# Revit family: Signalizator magnitokontaktnyy SMK-11
name_source: partatom
category: Датчики
units: mm (PartAtom-declared; Revit-internal decimal feet)

## family parameters
Всегда вертикально = Да
Заголовок OmniClass = Communication and Data Processing Equipment
На основе рабочей плоскости = Нет
Номер OmniClass = 23.85.50.17
Общий = Нет
При загрузке вырезать с полостями = Нет
Размер круглого соединителя = Использовать диаметр
Сохранять ориентацию аннотаций = Нет
Тип детали = Нормальный
Точка принадлежности помещению = Нет

## types (2) — shared parameters
ADSK_Единица измерения = шт.
ADSK_Завод-изготовитель = ООО НПП «МАГНИТО-КОНТАКТ»
ADSK_Материал = Пластик
ADSK_Обозначение = АТФЕ.425119.169 ПС
ADSK_Примечание = По устойчивости к климатическим воздействиям сигнализатор рассчитан для категории размещения III по ГОСТ 54455-2011 в диапазоне температур окружающего воздуха от -60°С до +60°С и относительной влажности до 98% при температуре +35°С без конденсации влаги.
ADSK_Размер_ДиаметрИзделия = 7 мм
ADSK_Размер_Длина = 22 мм
URL = https://m-kontakt.ru
Диапазон коммутируемого тока = от 0.005 до 0.25
Диапазон напряжений = от 0.05 до 72 (постоянного или переменного тока)
Длина вывода, м = 1 мм
Изготовитель = ООО НПП «МАГНИТО-КОНТАКТ»
Кабель = Да
Описание = Сигнализатор магнитоконтактный СМК-11 предназначен для применения в системах автоматики различных устройств, в технике бытового, коммерческого, медицинского, научного и промышленного назначений с выдачей сигнала, путем размыкания сухого контакта геркона, а так же в системах охранной или охранно-пожарной сигнализаций с целью блокировки элементов конструкций из немагнитопроводных материалов.
Срок службы = не менее 8 лет
Степень защиты = IP66/IP68
Тип применяемого геркона = Нормально разомкнутый (NO)
zero-valued in all types: Отметка по умолчанию

## per-type parameters (varying)
| type | Расстояние срабатывания/отпускания на магнитопроводящем основании, мм | Расстояние срабатывания/отпускания на немагнитопроводящем основании, мм |
| Сигнализатор магнитоконтактный СМК-11 | 10/13 | 5/7 |
| Сигнализатор магнитоконтактный СМК-11 усиленный | 14/17 | 6/8 |

note: column(s) folded — value = type name in every type: ADSK_Наименование
